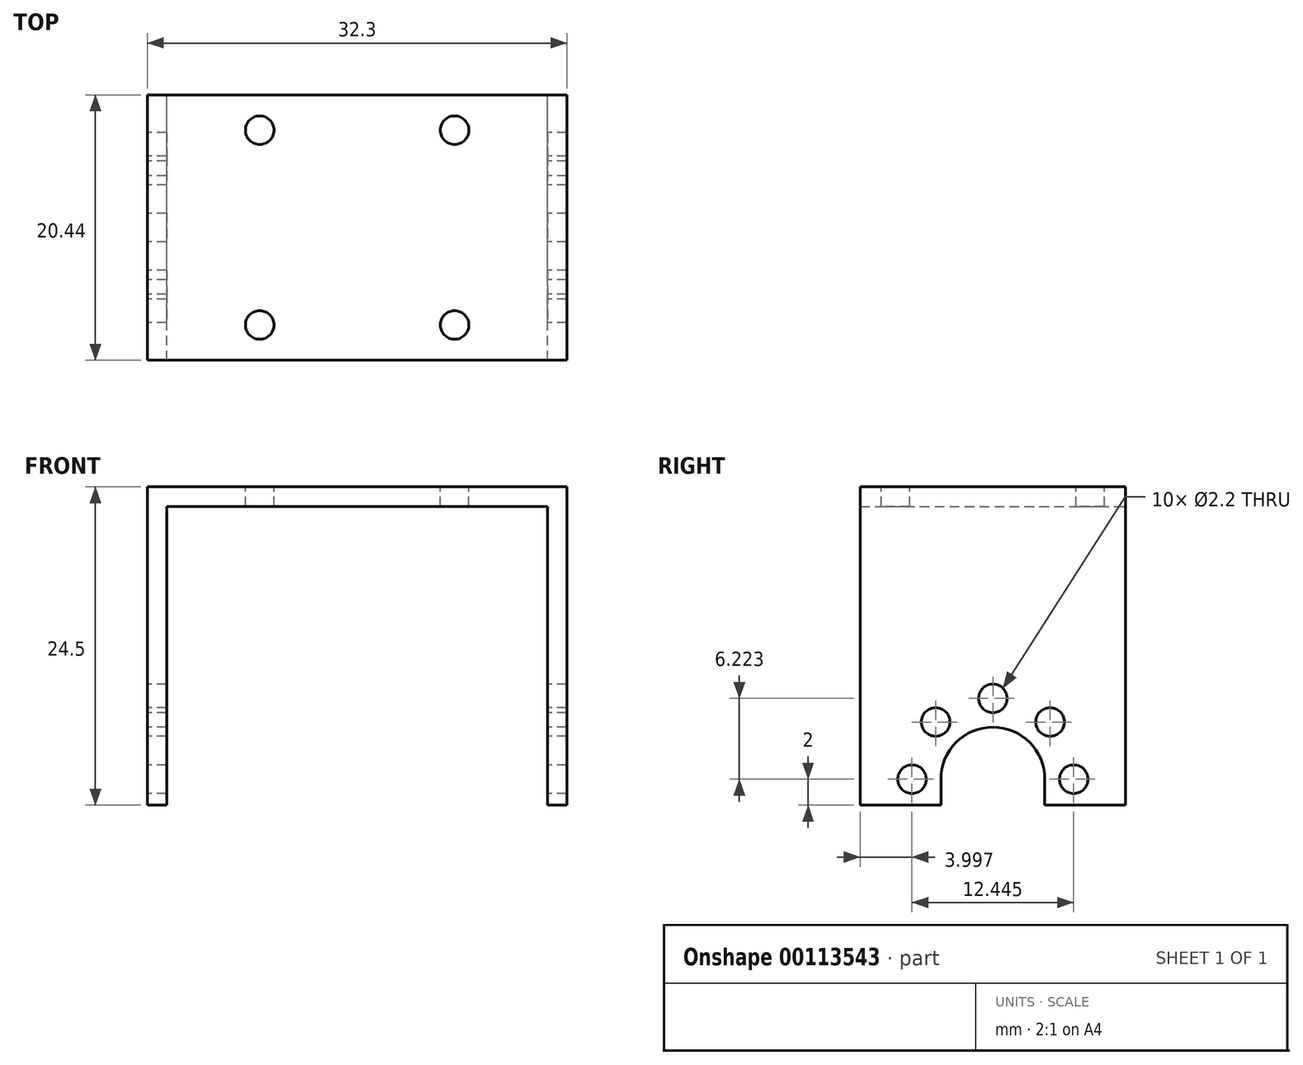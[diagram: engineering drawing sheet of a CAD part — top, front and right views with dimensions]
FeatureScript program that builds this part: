
annotation { "Feature Type Name" : "Feature", "Feature Type Description" : "" }
export const myFeature = defineFeature(function(context is Context, id is Id, definition is map)
    precondition{}
    {
        {
            var Q0;
            Q0=qCreatedBy(makeId("Front.planeOp"),FACE);
            var sketch = newSketch(context, id + "F0", { "sketchPlane" : qUnion([Q0])});
            skLineSegment(sketch, "E0.bottom", {"start": v(0, 0) * mm, "end": v(1.5, 0) * mm});
            skLineSegment(sketch, "E0.top", {"start": v(0, 24.5) * mm, "end": v(32.3, 24.5) * mm});
            skLineSegment(sketch, "E0.left", {"start": v(0, 0) * mm, "end": v(0, 24.5) * mm});
            skLineSegment(sketch, "E0.right", {"start": v(32.3, 0) * mm, "end": v(32.3, 24.5) * mm});
            skLineSegment(sketch, "E1.top", {"start": v(1.5, 23) * mm, "end": v(30.8, 23) * mm});
            skLineSegment(sketch, "E1.left", {"start": v(1.5, 0) * mm, "end": v(1.5, 23) * mm});
            skLineSegment(sketch, "E1.right", {"start": v(30.8, 0) * mm, "end": v(30.8, 23) * mm});
            skLineSegment(sketch, "E2.trimOffspring", {"start": v(30.8, 0) * mm, "end": v(32.3, 0) * mm});
            skSolve(sketch);
        }
        {
            var Q0;
            Q0=qSketchRegion(id+"F0",true);
            extrude(context, id + "F1", {"entities" : qUnion([Q0]), "depth" : 33 * mm});
        }
        {
            var Q0;
            Q0=makeQuery(id+"F1.opExtrude","SWEPT_FACE",FACE,{"disambiguationData":[OSD([sQuery(id+"F0.wireOp",EDGE,"E0.left")])]});
            var sketch = newSketch(context, id + "F2", { "sketchPlane" : qUnion([Q0])});
            skArc(sketch, "E3", {"start": v(20.5, 2) * mm, "mid": v(16.5, 6) * mm, "end": v(12.5, 2) * mm});
            skCircle(sketch, "E4", {"center": v(22.72, 2) * mm, "radius": 1.1 * mm});
            skCircle(sketch, "E5.1.0", {"center": v(20.9, 6.4) * mm, "radius": 1.1 * mm});
            skCircle(sketch, "E5.2.0", {"center": v(16.5, 8.22) * mm, "radius": 1.1 * mm});
            skCircle(sketch, "E5.3.0", {"center": v(12.1, 6.4) * mm, "radius": 1.1 * mm});
            skCircle(sketch, "E5.4.0", {"center": v(10.28, 2) * mm, "radius": 1.1 * mm});
            skLineSegment(sketch, "E6", {"start": v(12.5, 2) * mm, "end": v(12.5, 0) * mm});
            skLineSegment(sketch, "E7", {"start": v(20.5, 2) * mm, "end": v(20.5, 0) * mm});
            skLineSegment(sketch, "E8", {"start": v(12.5, 0) * mm, "end": v(20.5, 0) * mm});
            skLineSegment(sketch, "E9", {"start": v(16.5, 24.5) * mm, "end": v(16.5, 0) * mm, "construction": true});
            skPoint(sketch, "E10", {"position": v(16.5, 0) * mm});
            skLineSegment(sketch, "E11", {"start": v(6.28, 0) * mm, "end": v(0, 23) * mm});
            skLineSegment(sketch, "E12", {"start": v(6.28, 0) * mm, "end": v(0, 0) * mm});
            skLineSegment(sketch, "E13", {"start": v(0, 0) * mm, "end": v(0, 23) * mm});
            skLineSegment(sketch, "E14.MirrorCS", {"start": v(33, 0) * mm, "end": v(33, 23) * mm});
            skLineSegment(sketch, "E15.MirrorCS", {"start": v(26.72, 0) * mm, "end": v(33, 23) * mm});
            skLineSegment(sketch, "E16.MirrorCS", {"start": v(26.72, 0) * mm, "end": v(33, 0) * mm});
            skLineSegment(sketch, "E17.bottom", {"start": v(33, 0) * mm, "end": v(26.72, 0) * mm});
            skLineSegment(sketch, "E17.top", {"start": v(33, 23) * mm, "end": v(26.72, 23) * mm});
            skLineSegment(sketch, "E17.right", {"start": v(26.72, 0) * mm, "end": v(26.72, 23) * mm});
            skLineSegment(sketch, "E18.MirrorCS", {"start": v(0, 23) * mm, "end": v(6.28, 23) * mm});
            skLineSegment(sketch, "E19.MirrorCS", {"start": v(6.28, 0) * mm, "end": v(6.28, 23) * mm});
            skLineSegment(sketch, "E20.bottom", {"start": v(33, 24.5) * mm, "end": v(26.72, 24.5) * mm});
            skLineSegment(sketch, "E20.left", {"start": v(33, 24.5) * mm, "end": v(33, 23) * mm});
            skLineSegment(sketch, "E20.right", {"start": v(26.72, 24.5) * mm, "end": v(26.72, 23) * mm});
            skLineSegment(sketch, "E21.top", {"start": v(0, 24.5) * mm, "end": v(6.28, 24.5) * mm});
            skLineSegment(sketch, "E21.left", {"start": v(0, 23) * mm, "end": v(0, 24.5) * mm});
            skLineSegment(sketch, "E21.right", {"start": v(6.28, 23) * mm, "end": v(6.28, 24.5) * mm});
            skSolve(sketch);
        }
        {
            var Q0;
            Q0=qSketchRegion(id+"F2",true);
            extrude(context, id + "F3", {"entities" : qUnion([Q0]), "operationType" : NewBodyOperationType.REMOVE, "endBound" : BoundingType.THROUGH_ALL, "oppositeDirection" : true, "depth" : 25 * mm});
        }
        {
            var Q0;
            Q0=makeQuery(id+"F1.opExtrude","SWEPT_FACE",FACE,{"disambiguationData":[OSD([sQuery(id+"F0.wireOp",EDGE,"E0.top")])]});
            var sketch = newSketch(context, id + "F4", { "sketchPlane" : qUnion([Q0])});
            skLineSegment(sketch, "E22", {"start": v(16.15, -6.28) * mm, "end": v(16.15, -26.72) * mm, "construction": true});
            skLineSegment(sketch, "E23", {"start": v(0, -16.5) * mm, "end": v(32.3, -16.5) * mm, "construction": true});
            skCircle(sketch, "E24", {"center": v(8.65, -9) * mm, "radius": 1.1 * mm});
            skCircle(sketch, "E25.MirrorC", {"center": v(23.65, -9) * mm, "radius": 1.1 * mm});
            skCircle(sketch, "E26.MirrorC", {"center": v(8.65, -24) * mm, "radius": 1.1 * mm});
            skCircle(sketch, "E27.MirrorC", {"center": v(23.65, -24) * mm, "radius": 1.1 * mm});
            skLineSegment(sketch, "E28.0", {"start": v(32.3, -6.28) * mm, "end": v(0, -6.28) * mm, "construction": true});
            skLineSegment(sketch, "E29.0", {"start": v(32.3, -26.72) * mm, "end": v(0, -26.72) * mm, "construction": true});
            skPoint(sketch, "E30", {"position": v(16.15, -6.28) * mm});
            skSolve(sketch);
        }
        {
            var Q0;
            Q0=qSketchRegion(id+"F4",true);
            extrude(context, id + "F5", {"entities" : qUnion([Q0]), "operationType" : NewBodyOperationType.REMOVE, "endBound" : BoundingType.UP_TO_NEXT, "oppositeDirection" : true, "depth" : 25 * mm});
        }
    });
